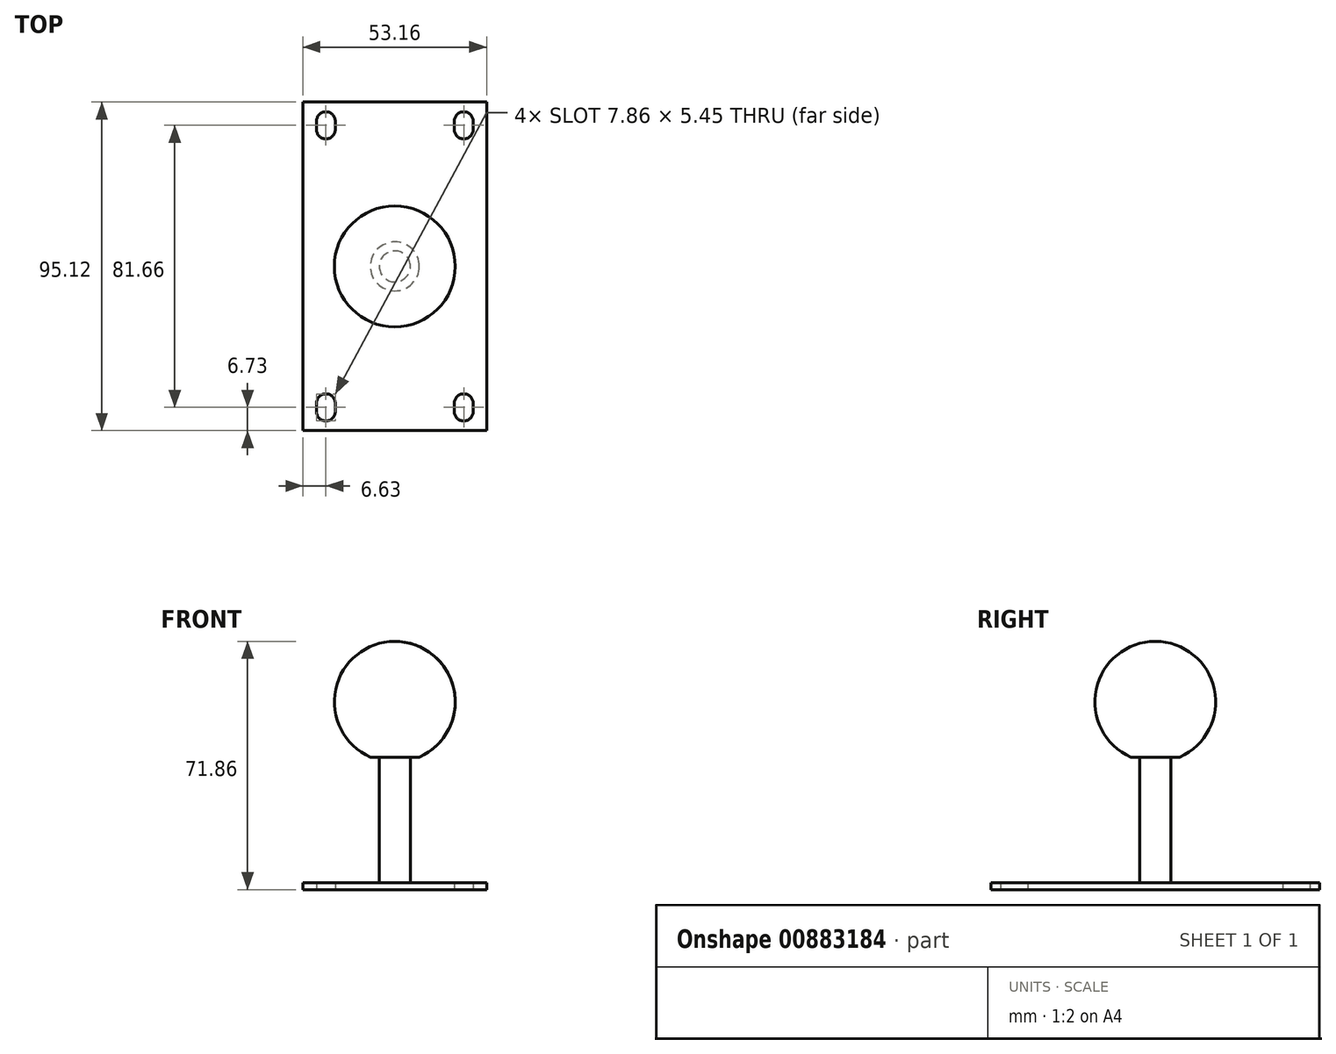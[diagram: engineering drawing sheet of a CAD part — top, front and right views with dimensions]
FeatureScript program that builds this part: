
annotation { "Feature Type Name" : "Feature", "Feature Type Description" : "" }
export const myFeature = defineFeature(function(context is Context, id is Id, definition is map)
    precondition{}
    {
        {
            var Q0;
            Q0=qCreatedBy(makeId("Top.planeOp"),FACE);
            var sketch = newSketch(context, id + "F0", { "sketchPlane" : qUnion([Q0])});
            skLineSegment(sketch, "E0.bottom", {"start": v(26.57, 47.56) * mm, "end": v(-26.58, 47.56) * mm});
            skLineSegment(sketch, "E0.top", {"start": v(26.58, -47.56) * mm, "end": v(-26.57, -47.56) * mm});
            skLineSegment(sketch, "E0.left", {"start": v(26.57, 47.56) * mm, "end": v(26.58, -47.56) * mm});
            skLineSegment(sketch, "E0.right", {"start": v(-26.58, 47.56) * mm, "end": v(-26.57, -47.56) * mm});
            skPoint(sketch, "E0.middle", {"position": v(0, 0) * mm});
            skLineSegment(sketch, "E1.bottom", {"start": v(-17.23, 39.62) * mm, "end": v(-22.68, 39.62) * mm});
            skLineSegment(sketch, "E1.top", {"start": v(-17.23, 42.03) * mm, "end": v(-22.68, 42.03) * mm});
            skLineSegment(sketch, "E1.left", {"start": v(-17.23, 39.62) * mm, "end": v(-17.23, 42.03) * mm});
            skLineSegment(sketch, "E1.right", {"start": v(-22.68, 39.62) * mm, "end": v(-22.68, 42.03) * mm});
            skPoint(sketch, "E1.middle", {"position": v(-19.95, 40.83) * mm});
            skArc(sketch, "E2", {"start": v(-22.68, 39.62) * mm, "mid": v(-19.95, 36.9) * mm, "end": v(-17.23, 39.62) * mm});
            skArc(sketch, "E3", {"start": v(-22.68, 42.03) * mm, "mid": v(-19.95, 44.76) * mm, "end": v(-17.23, 42.03) * mm});
            skArc(sketch, "E4.MirrorCS", {"start": v(22.68, 42.03) * mm, "mid": v(19.95, 44.76) * mm, "end": v(17.23, 42.03) * mm});
            skLineSegment(sketch, "E5.MirrorCS", {"start": v(22.68, 39.62) * mm, "end": v(22.68, 42.03) * mm});
            skLineSegment(sketch, "E6.MirrorCS", {"start": v(17.23, 39.62) * mm, "end": v(17.23, 42.03) * mm});
            skArc(sketch, "E7.MirrorCS", {"start": v(22.68, 39.62) * mm, "mid": v(19.95, 36.9) * mm, "end": v(17.23, 39.62) * mm});
            skArc(sketch, "E8.MirrorCS", {"start": v(22.68, -39.62) * mm, "mid": v(19.95, -36.9) * mm, "end": v(17.23, -39.62) * mm});
            skLineSegment(sketch, "E9.MirrorCS", {"start": v(17.23, -39.62) * mm, "end": v(17.23, -42.03) * mm});
            skLineSegment(sketch, "E10.MirrorCS", {"start": v(22.68, -39.62) * mm, "end": v(22.68, -42.03) * mm});
            skArc(sketch, "E11.MirrorCS", {"start": v(22.68, -42.03) * mm, "mid": v(19.95, -44.76) * mm, "end": v(17.23, -42.03) * mm});
            skArc(sketch, "E12.MirrorCS", {"start": v(-22.68, -39.62) * mm, "mid": v(-19.95, -36.9) * mm, "end": v(-17.23, -39.62) * mm});
            skLineSegment(sketch, "E13.MirrorCS", {"start": v(-22.68, -39.62) * mm, "end": v(-22.68, -42.03) * mm});
            skLineSegment(sketch, "E14.MirrorCS", {"start": v(-17.23, -39.62) * mm, "end": v(-17.23, -42.03) * mm});
            skArc(sketch, "E15.MirrorCS", {"start": v(-22.68, -42.03) * mm, "mid": v(-19.95, -44.76) * mm, "end": v(-17.23, -42.03) * mm});
            skSolve(sketch);
        }
        {
            var Q0;
            Q0 = qSketchRegion(id + "F0", true);
            extrude(context, id + "F1", {"entities" : qUnion([Q0]), "depth" : 2 * mm, "offsetDistance" : 25 * mm});
        }
        {
            var Q0;
            Q0=makeQuery(id+"F1.opExtrude","CAP_FACE",FACE,{"disambiguationData":[OSD([sQuery(id+"F0.wireOp",EDGE,"E0.bottom"),sQuery(id+"F0.wireOp",EDGE,"E0.top"),sQuery(id+"F0.wireOp",EDGE,"E0.left"),sQuery(id+"F0.wireOp",EDGE,"E0.right"),sQuery(id+"F0.wireOp",EDGE,"E1.left"),sQuery(id+"F0.wireOp",EDGE,"E1.right"),sQuery(id+"F0.wireOp",EDGE,"E2"),sQuery(id+"F0.wireOp",EDGE,"E3"),sQuery(id+"F0.wireOp",EDGE,"E4.MirrorCS"),sQuery(id+"F0.wireOp",EDGE,"E5.MirrorCS"),sQuery(id+"F0.wireOp",EDGE,"E6.MirrorCS"),sQuery(id+"F0.wireOp",EDGE,"E7.MirrorCS"),sQuery(id+"F0.wireOp",EDGE,"E8.MirrorCS"),sQuery(id+"F0.wireOp",EDGE,"E9.MirrorCS"),sQuery(id+"F0.wireOp",EDGE,"E10.MirrorCS"),sQuery(id+"F0.wireOp",EDGE,"E11.MirrorCS"),sQuery(id+"F0.wireOp",EDGE,"E12.MirrorCS"),sQuery(id+"F0.wireOp",EDGE,"E13.MirrorCS"),sQuery(id+"F0.wireOp",EDGE,"E14.MirrorCS"),sQuery(id+"F0.wireOp",EDGE,"E15.MirrorCS")])],"isStart":false});
            var sketch = newSketch(context, id + "F2", { "sketchPlane" : qUnion([Q0])});
            skCircle(sketch, "E16", {"center": v(0, 0) * mm, "radius": 4.5 * mm});
            skSolve(sketch);
        }
        {
            var Q0;
            Q0 = qSketchRegion(id + "F2", true);
            extrude(context, id + "F3", {"entities" : qUnion([Q0]), "operationType" : NewBodyOperationType.ADD, "depth" : 36.36 * mm, "offsetDistance" : 25 * mm});
        }
        {
            var Q0;
            Q0=qCreatedBy(makeId("Front.planeOp"),FACE);
            var sketch = newSketch(context, id + "F4", { "sketchPlane" : qUnion([Q0])});
            skArc(sketch, "E17", {"start": v(7.09, 38.36) * mm, "mid": v(17.12, 57.98) * mm, "end": v(0, 71.86) * mm});
            skLineSegment(sketch, "E18", {"start": v(0, 71.86) * mm, "end": v(0, 38.36) * mm});
            skLineSegment(sketch, "E19", {"start": v(0, 38.36) * mm, "end": v(7.09, 38.36) * mm});
            skSolve(sketch);
        }
        {
            var Q0;
            Q0 = qSketchRegion(id + "F4", true);
            var Q1;
            Q1=sQuery(id+"F4.wireOp",EDGE,"E18");
            revolve(context, id + "F5", {"operationType" : NewBodyOperationType.ADD, "surfaceOperationType" : NewSurfaceOperationType.NEW, "entities" : qUnion([Q0]), "axis" : qUnion([Q1]), "revolveType" : RevolveType.FULL});
        }
    });
